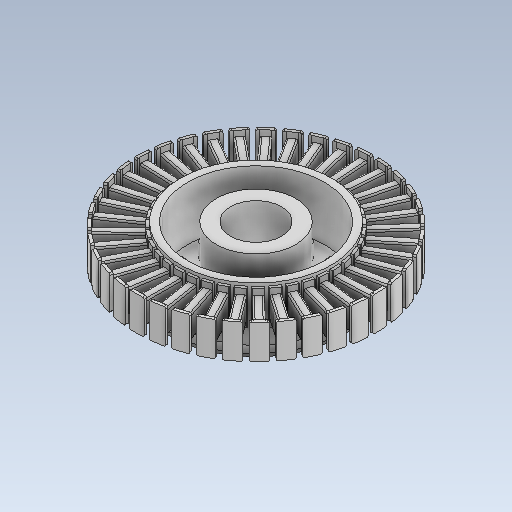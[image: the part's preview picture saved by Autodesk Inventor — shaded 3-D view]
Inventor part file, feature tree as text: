
AUTODESK INVENTOR PART (.ipt)
format: ipt  version: 2020 (Build 240168000, 168)  size: 1,930,240 bytes
history: native  units: mm
features: extrude x17, sketch x17, projected_geometry x15, pattern_circular x5, fillet x5, thicken_offset x2, plane x2, chamfer x1
ambient origin geometry x8: Origin, YZ Plane, XZ Plane, XY Plane, X Axis, Y Axis, Z Axis, Center Point
bodies: Solid1 (feature_tree)
feature tree (64):
  extrude  "Extrusion1"  Depth=24.0mm
  extrude  "Extrusion2"  Depth=1.0mm
  extrude  "Extrusion3"  Depth=18.0mm
  thicken_offset  "Thicken1"
  extrude  "Extrusion4"  Depth=1.0mm
  extrude  "Extrusion5"  Depth=1.0mm
  plane  "Work Plane1"
  extrude  "Extrusion6"  Depth=1.0mm
  extrude  "Extrusion7"  Depth=1.0mm TaperAngle=0.0deg
  extrude  "Extrusion8"  Depth=6.0mm
  pattern_circular  "Circular Pattern1"  [2 undecoded]
  fillet  "Fillet1"  Radius=2.0mm
  pattern_circular  "Circular Pattern2"  [2 undecoded]
  extrude  "Extrusion9"  Depth=6.0mm TaperAngle=360.0deg
  pattern_circular  "Circular Pattern3"  [2 undecoded]
  extrude  "Extrusion10"  Depth=6.0mm TaperAngle=360.0deg
  pattern_circular  "Circular Pattern4"  [2 undecoded]
  extrude  "Extrusion11"  Depth=6.0mm
  fillet  "Fillet2"  Radius=2.0mm
  fillet  "Fillet3"  Radius=40.0mm
  pattern_circular  "Circular Pattern5"  [2 undecoded]
  extrude  "Extrusion12"  TaperAngle=135.0deg  [1 undecoded]
  extrude  "Extrusion13"  Depth=3.0mm
  extrude  "Extrusion14"  Depth=1.0mm TaperAngle=0.0deg
  fillet  "Fillet4"  Radius=40.0mm
  extrude  "Extrusion15"  Depth=30.0mm
  chamfer  "Chamfer1"  Distance=47.0mm
  thicken_offset  "Thicken2"
  plane  "Work Plane2"
  extrude  "Extrusion16"  TaperAngle=22.5deg  [1 undecoded]
  fillet  "Fillet5"  Radius=2.094395mm
  extrude  "Extrusion17"  Depth=6.0mm
  sketch  "Sketch1"  dims[d0=60.0mm d1=24.0mm]
  sketch  "Sketch2"  dims[d2=1.0mm d3=0.0mm d4=28.0mm]
  projected_geometry  "Projected Loop1"
  sketch  "Sketch3"  dims[d5=19.0mm d6=0.0mm d7=18.0mm]
  projected_geometry  "Projected Loop2"
  sketch  "Sketch4"  dims[d8=2.5mm d9=0.0mm d10=1.0mm]
  projected_geometry  "Projected Loop3"
  sketch  "Sketch5"  dims[d11=1.0mm d12=16.0mm]
  projected_geometry  "Projected Loop4"
  sketch  "Sketch6"  dims[d13=1.0mm d14=0.0mm d15=53.0mm]
  projected_geometry  "Projected Loop5"
  sketch  "Sketch7"  dims[d16=48.0mm d17=1.0mm d18=0.0mm]
  projected_geometry  "Projected Loop6"
  sketch  "Sketch8"  dims[d19=6.0mm d20=84.0mm]
  projected_geometry  "Projected Loop7"
  sketch  "Sketch9"  dims[d21=82.0mm]
  projected_geometry  "Projected Loop8"
  sketch  "Sketch10"  dims[d22=53.0mm]
  projected_geometry  "Projected Loop9"
  sketch  "Sketch11"  dims[d23=55.0mm]
  projected_geometry  "Projected Loop10"
  sketch  "Sketch12"  dims[d24=1.5mm]
  sketch  "Sketch13"  dims[d25=1.5mm]
  projected_geometry  "Projected Loop11"
  sketch  "Sketch14"  dims[d26=42.0mm]
  projected_geometry  "Projected Loop12"
  sketch  "Sketch15"  dims[d27=15.097098mm]
  projected_geometry  "Projected Loop13"
  sketch  "Sketch16"  dims[d28=42.0mm]
  projected_geometry  "Projected Loop14"
  sketch  "Sketch17"  dims[d29=16.318829mm d30=12.0mm d31=0.0mm d32=2.0mm d33=0.0mm d34=2.0mm d35=0.0mm d36=390.0mm d37=360.0deg d39=0.5mm d40=390.0mm d41=360.0deg d43=16.0mm d44=4.0mm d45=2.0mm d46=0.0mm d47=40.0mm d48=360.0deg d50=15.0mm d51=135.0deg d52=3.0mm d53=1.0mm d54=0.0mm d55=40.0mm d56=360.0deg d58=30.0mm d59=47.0mm d60=22.5deg d61=2.094395mm d62=2.094395mm d63=1.0mm d64=0.0mm d65=1.5mm d66=1.0mm d67=80.0mm d68=360.0deg d70=2.0mm d71=100.0mm d72=0.0mm d73=18.0mm d74=15.0mm d75=0.0mm d76=6.0mm d77=6.0mm d78=6.0mm d79=6.0mm d80=5.0mm d81=0.0mm d82=1.0mm d83=12.0mm d84=16.0mm d85=20.0mm d86=24.0mm d87=15.0deg d88=15.0deg d89=2.0mm d90=0.0mm d91=1.0mm d92=2.0mm d93=45.0deg d94=1.0mm d95=1.0mm d96=13.0mm d97=1.0mm d98=20.0mm d99=0.0mm d100=3.0mm d101=7.0mm d102=2.6mm d103=6.0mm d104=4.0mm d105=0.0mm]
  projected_geometry  "Projected Loop15"
note: 12 required parameter values undecoded (feature->parameter linkage not recoverable at this tier; creation-order binding heuristic only, values carry confidence <= 0.55)
